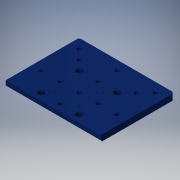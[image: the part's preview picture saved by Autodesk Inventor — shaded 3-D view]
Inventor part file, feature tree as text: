
AUTODESK INVENTOR PART (.ipt)
format: ipt  version: 2019.4 (Build 234330000, 330)  size: 166,912 bytes
history: native  units: in
note: dims shown in document units (in); Inventor stores cm internally (conversion verified against a paired STEP export)
features: chamfer x2, direct_edit x1, move_body x1
ambient origin geometry x8: Origin, YZ Plane, XZ Plane, XY Plane, X Axis, Y Axis, Z Axis, Center Point
bodies: Solid1 (feature_tree)
feature tree (4):
  direct_edit  "Direct Edit1"
  chamfer  "Chamfer2"  [1 undecoded]
  chamfer  "Chamfer1"  Distance=0.0787in Angle=45.0deg
  move_body  "Move1"
note: 1 required parameter value undecoded (feature->parameter linkage not recoverable at this tier; creation-order binding heuristic only, values carry confidence <= 0.55)
